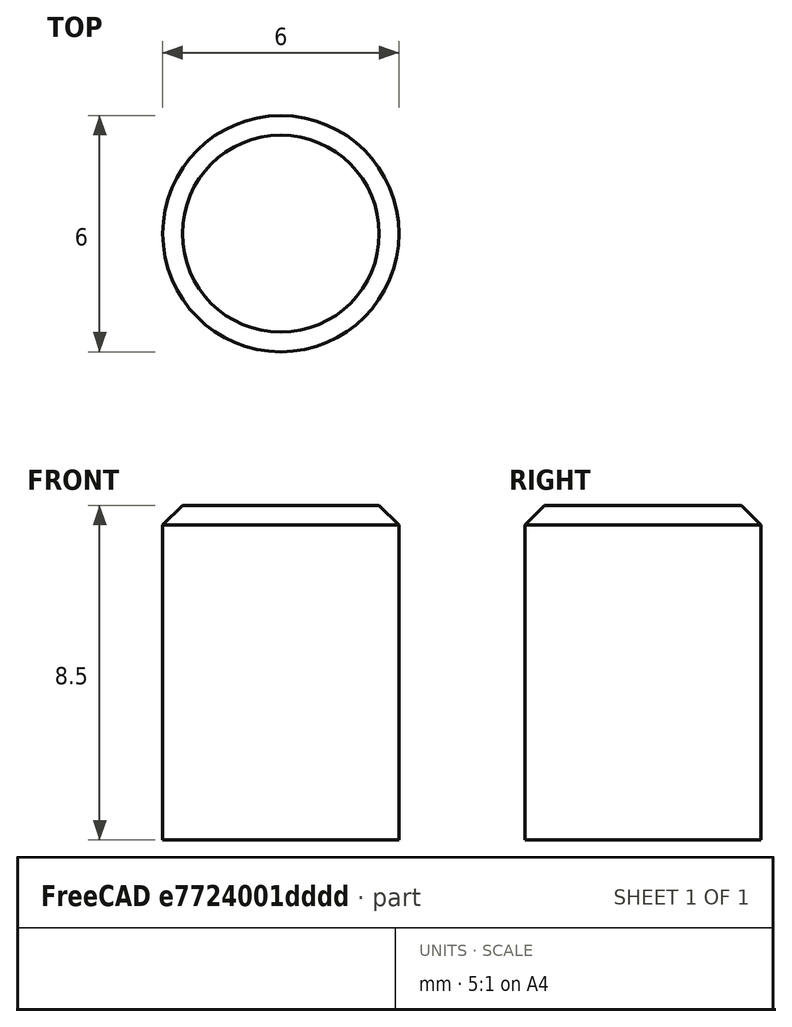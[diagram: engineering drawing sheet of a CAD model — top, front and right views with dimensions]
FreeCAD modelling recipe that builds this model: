
FCSTD DOCUMENT  (FreeCAD 0.19R16699 (Git))
Label: RD901F_Shaft_15R
License: All rights reserved
LicenseURL: http://en.wikipedia.org/wiki/All_rights_reserved
objects: Sketcher::SketchObject×1, PartDesign::Pad×1, PartDesign::Chamfer×1, PartDesign::Body×1
note: 5 computed .brp shape members not serialized (recipe doc carries the construction recipe); baked Part::Feature solids carry a one-line shape summary decoded from their .brp

FEATURE [Sketcher::SketchObject] Sketch
  MapMode = 5
  Support = -> [XY_Plane]
  sketch-geometry (1):
    g0: Circle CenterX=0 CenterY=0 CenterZ=0 NormalX=0 NormalY=0 NormalZ=1 AngleXU=0 Radius=3
  constraints (2):
    c: Coincident(g0,g-1)
    c: Radius(g0) = 3
FEATURE [PartDesign::Pad] Pad
  Length = 8.5
  Length2 = 100
  Profile = -> Sketch
  Type = 0
FEATURE [PartDesign::Chamfer] Chamfer
  Base = -> Pad [Edge3]
  BaseFeature = -> Pad
  Size = 0.5
FEATURE [PartDesign::Body] Body  label="RD901F_Shaft_15R"
  Group = -> [Sketch,Pad,Chamfer]
  Origin = -> Origin
  Tip = -> Chamfer
